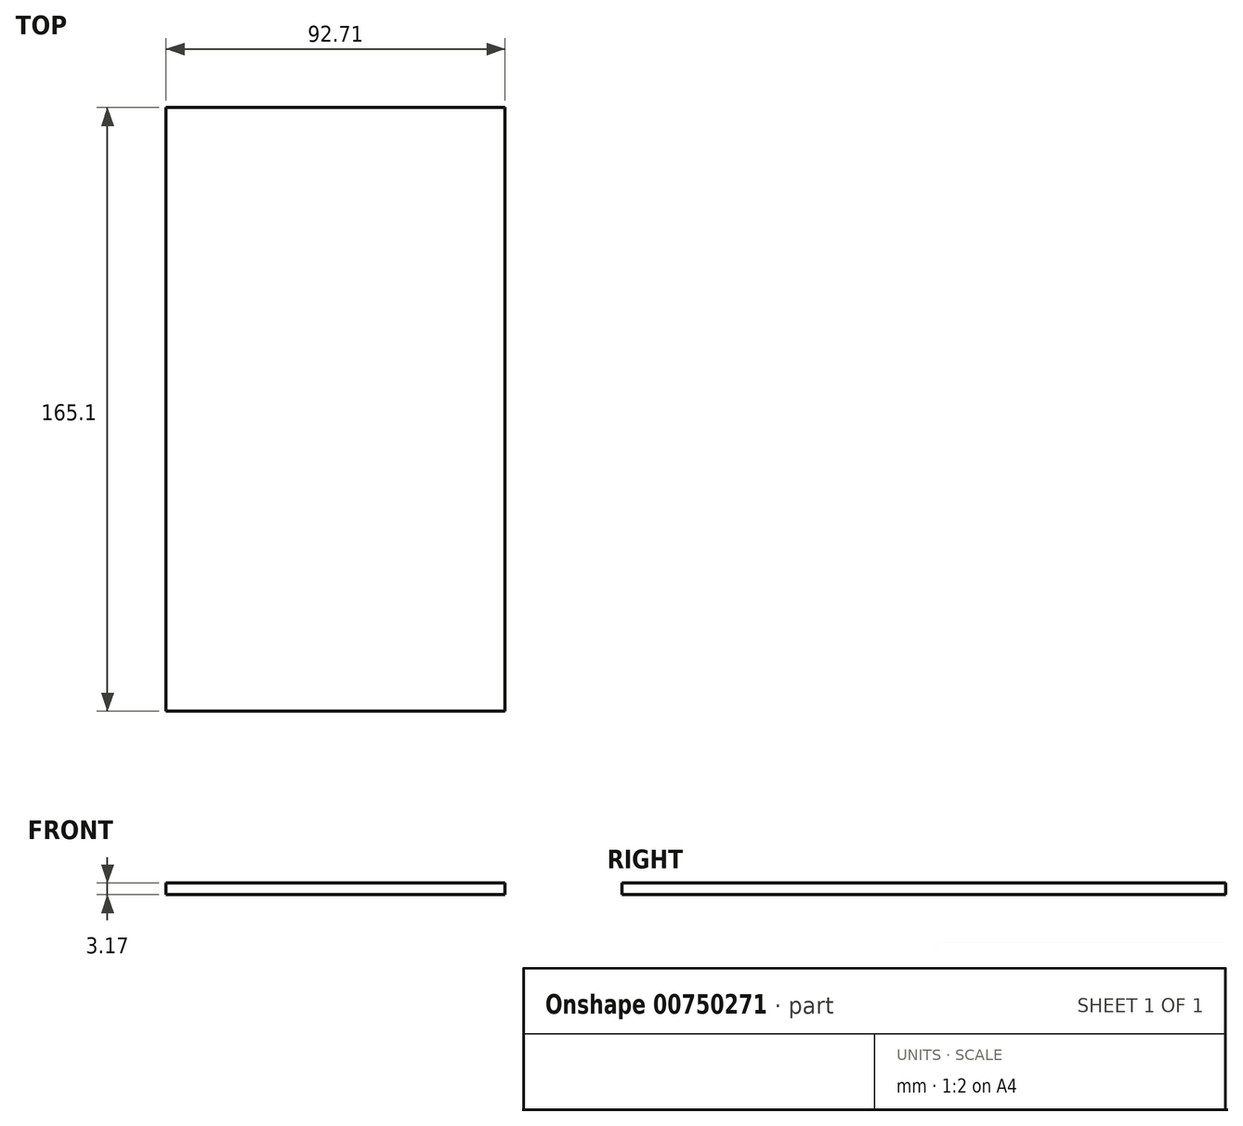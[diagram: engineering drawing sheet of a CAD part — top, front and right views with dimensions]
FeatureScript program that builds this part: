
annotation { "Feature Type Name" : "Feature", "Feature Type Description" : "" }
export const myFeature = defineFeature(function(context is Context, id is Id, definition is map)
    precondition{}
    {
        {
            var Q0;
            Q0=qCreatedBy(makeId("Top.planeOp"),FACE);
            var sketch = newSketch(context, id + "F0", { "sketchPlane" : qUnion([Q0])});
            skLineSegment(sketch, "E0", {"start": v(-76.88, 91.33) * mm, "end": v(-76.88, -73.77) * mm});
            skLineSegment(sketch, "E1", {"start": v(-76.88, -73.77) * mm, "end": v(-169.6, -73.77) * mm});
            skLineSegment(sketch, "E2", {"start": v(-169.6, -73.77) * mm, "end": v(-169.6, 91.33) * mm});
            skLineSegment(sketch, "E3", {"start": v(-169.6, 91.33) * mm, "end": v(-76.88, 91.33) * mm});
            skSolve(sketch);
        }
        {
            var Q0;
            Q0=makeQuery(id+"F0.imprint","IMPRINT",FACE,{"disambiguationData":[TD([[makeQuery(id+"F0.imprint","IMPRINT",EDGE,{"derivedFrom":sQuery(id+"F0.wireOp",EDGE,"E0")}),-1.0]])]});
            extrude(context, id + "F1", {"entities" : qUnion([Q0]), "oppositeDirection" : true, "depth" : 3.17 * mm, "offsetDistance" : 25.4 * mm});
        }
    });
